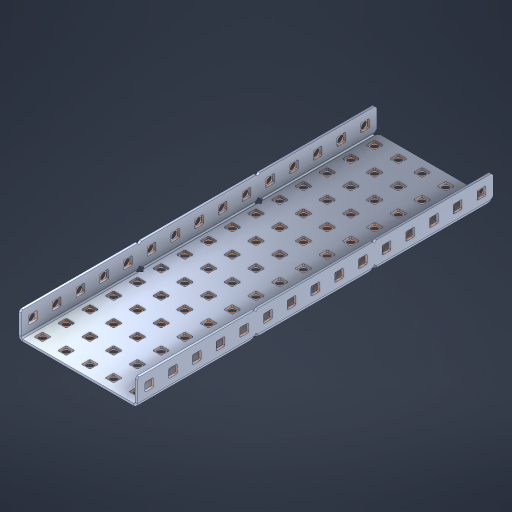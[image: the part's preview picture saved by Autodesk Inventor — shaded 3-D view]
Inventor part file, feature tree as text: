
AUTODESK INVENTOR PART (.ipt)
format: ipt  version: 2023 (Build 270158000, 158)  size: 1,352,192 bytes
history: native  units: in
note: dims shown in document units (in); Inventor stores cm internally (conversion verified against a paired STEP export)
features: other x110, extrude x104, sheet_metal_op x10, sketch x8, mirror x1, pattern_linear x1, chamfer x1
ambient origin geometry x8: Origin, YZ Plane, XZ Plane, XY Plane, X Axis, Y Axis, Z Axis, Center Point
bodies: Solid1 (feature_tree), Body (feature_tree)
feature tree (235):
  other  "Flange Pattern Plane"
  sheet_metal_op  "Flange Pattern"
  sheet_metal_op  "Body Pattern"
  other  "Arc Length"
  mirror  "Notch Mirror"
  pattern_linear  "Notch Pattern"  Spacing1=0.1875in  [1 undecoded]
  chamfer  "End Chamfer"
  extrude  "Half Cut"  Depth=0.0469in
  sketch  "Sketch1"  dims[d0=2.5in]
  other  "Plate1"
  sketch  "Sketch2"  dims[d1=7.5in]
  other  "Plate2"
  sheet_metal_op  "Bend1"
  sheet_metal_op  "Corner1"
  sketch  "Sketch3"  dims[d2=0.0469in]
  other  "Flange Pattern Sketch"
  sketch  "Sketch7"  dims[d3=0.0469in]
  other  "Srf1"
  other  "Srf2"
  sketch  "Sketch8"  dims[d4=0.0234in]
  sketch  "Sketch9"  dims[d5=0.0938in]
  other  "Srf91"
  sheet_metal_op  "Body Pattern Sketch"
  other  "Srf92"
  sketch  "Sketch13"  dims[d6=0.0469in]
  sketch  "Sketch14"  dims[d7=0.5in d8=90.0deg d9=0.0312in d10=0.1875in d11=0.0469in d12=0.0469in d16=0.182in d17=0.02in d18=0.0469in d19=0.0in d20=0.25in d21=0.25in d46=0.172in d47=1.0in d48=0.0in d49=0.182in d50=0.02in d51=0.25in d52=0.25in d53=0.0469in d54=0.0in d55=0.172in d56=1.0in d57=0.0in d60=5.9055in d62=0.5in d63=1.9685in d65=0.5in d85=0.1227in d86=0.1659in d88=0.04in d89=0.0469in d90=0.0in d91=0.04in d92=0.0491in d95=2.5in d96=0.04in d97=0.25in d98=45.0deg d101=0.0in d102=2.497in d131=2.5in d132=5.9055in d134=0.5in d139=0.5in]
  other  "Srf856"
  other  "Srf1310"
  other  "Srf1311"
  other  "Srf1312"
  other  "Srf1376"
  other  "Srf1377"
  other  "Srf1728"
  other  "Srf1755"
  other  "Srf1878"
  other  "Srf1879"
  other  "Srf1880"
  other  "Srf1881"
  other  "Srf1882"
  other  "Srf1883"
  other  "Srf1884"
  other  "Srf1885"
  other  "Srf1886"
  other  "Srf1887"
  other  "Srf1888"
  other  "Srf1889"
  other  "Srf1890"
  other  "Srf1891"
  other  "Srf1892"
  other  "Srf1893"
  other  "Srf1894"
  other  "Srf1895"
  other  "Srf1896"
  other  "Srf1897"
  other  "Srf1898"
  other  "Srf1899"
  other  "Srf1900"
  other  "Srf1901"
  other  "Srf1942"
  other  "Srf1943"
  other  "Srf1944"
  other  "Srf1945"
  other  "Srf1946"
  other  "Srf1947"
  other  "Srf1948"
  other  "Srf1949"
  other  "Srf1950"
  other  "Srf1951"
  other  "Srf1952"
  other  "Srf1953"
  other  "Srf1954"
  other  "Srf1955"
  other  "Srf1956"
  other  "Srf1957"
  other  "Srf1958"
  other  "Srf1959"
  other  "Srf1960"
  other  "Srf1961"
  other  "Srf1962"
  other  "Srf1963"
  other  "Srf1964"
  other  "Srf1965"
  other  "Srf1966"
  other  "Srf1967"
  other  "Srf1968"
  other  "Srf1969"
  other  "Srf1970"
  other  "Srf2146"
  other  "Srf2147"
  other  "Srf2148"
  other  "Srf2149"
  other  "Srf2150"
  other  "Srf2151"
  other  "Srf2152"
  other  "Srf2153"
  other  "Srf2154"
  other  "Srf2155"
  other  "Srf2156"
  other  "Srf2157"
  other  "Srf2158"
  other  "Srf2159"
  other  "Srf2160"
  other  "Srf2161"
  other  "Srf2162"
  other  "Srf2163"
  other  "Srf2164"
  other  "Srf2165"
  other  "Srf2166"
  other  "Srf2167"
  other  "Srf2168"
  other  "Srf2169"
  other  "Srf2170"
  other  "Srf2171"
  other  "Srf2172"
  other  "Srf2173"
  other  "Srf2174"
  other  "Srf2175"
  other  "Srf2176"
  other  "Srf2177"
  other  "Srf2178"
  other  "Srf2179"
  other  "Srf2180"
  other  "Srf2181"
  other  "Srf2182"
  other  "Srf2183"
  other  "Srf2184"
  other  "Srf2185"
  sheet_metal_op  "Flange Stamp"
  sheet_metal_op  "Flange Circle"
  sheet_metal_op  "Body Stamp"
  sheet_metal_op  "Body Circle"
  sheet_metal_op  "Notch"
  extrude  "ExtrusionSrf2"  Depth=0.0469in
  extrude  "ExtrusionSrf92"  Depth=2.5in
  extrude  "ExtrusionSrf856"  Depth=0.02in
  extrude  "ExtrusionSrf1310"  Depth=0.0469in
  extrude  "ExtrusionSrf1311"  TaperAngle=0.0deg  [1 undecoded]
  extrude  "ExtrusionSrf1312"  Depth=0.25in
  extrude  "ExtrusionSrf1376"  Depth=0.25in
  extrude  "ExtrusionSrf1377"  Depth=2.5in
  extrude  "ExtrusionSrf1728"  Depth=2.5in TaperAngle=0.0deg
  extrude  "ExtrusionSrf1755"  Depth=2.5in
  extrude  "ExtrusionSrf1878"  Depth=0.02in
  extrude  "ExtrusionSrf1879"  Depth=0.25in
  extrude  "ExtrusionSrf1880"  Depth=0.25in
  extrude  "ExtrusionSrf1881"  Depth=0.0469in
  extrude  "ExtrusionSrf1882"  TaperAngle=0.0deg  [1 undecoded]
  extrude  "ExtrusionSrf1883"  Depth=2.5in
  extrude  "ExtrusionSrf1884"  Depth=2.5in TaperAngle=0.0deg
  extrude  "ExtrusionSrf1885"  Depth=2.5in
  extrude  "ExtrusionSrf1886"  Depth=2.5in
  extrude  "ExtrusionSrf1887"  Depth=2.5in
  extrude  "ExtrusionSrf1888"  Depth=2.5in
  extrude  "ExtrusionSrf1889"  Depth=2.5in
  extrude  "ExtrusionSrf1890"  Depth=0.0469in
  extrude  "ExtrusionSrf1891"  TaperAngle=0.0deg  [1 undecoded]
  extrude  "ExtrusionSrf1892"  Depth=2.5in
  extrude  "ExtrusionSrf1893"  Depth=2.5in
  extrude  "ExtrusionSrf1894"  Depth=2.5in
  extrude  "ExtrusionSrf1895"  Depth=0.25in TaperAngle=45.0deg
  extrude  "ExtrusionSrf1896"  TaperAngle=0.0deg  [1 undecoded]
  extrude  "ExtrusionSrf1897"  Depth=2.5in
  extrude  "ExtrusionSrf1898"  Depth=2.5in
  extrude  "ExtrusionSrf1899"  Depth=2.5in
  extrude  "ExtrusionSrf1900"  Depth=2.5in
  extrude  "ExtrusionSrf1901"  Depth=2.5in
  extrude  "ExtrusionSrf1942"  [1 undecoded]
  extrude  "ExtrusionSrf1943"  [1 undecoded]
  extrude  "ExtrusionSrf1944"  [1 undecoded]
  extrude  "ExtrusionSrf1945"  [1 undecoded]
  extrude  "ExtrusionSrf1946"  [1 undecoded]
  extrude  "ExtrusionSrf1947"  [1 undecoded]
  extrude  "ExtrusionSrf1948"  [1 undecoded]
  extrude  "ExtrusionSrf1949"  [1 undecoded]
  extrude  "ExtrusionSrf1950"  [1 undecoded]
  extrude  "ExtrusionSrf1951"  [1 undecoded]
  extrude  "ExtrusionSrf1952"  [1 undecoded]
  extrude  "ExtrusionSrf1953"  [1 undecoded]
  extrude  "ExtrusionSrf1954"  [1 undecoded]
  extrude  "ExtrusionSrf1955"  [1 undecoded]
  extrude  "ExtrusionSrf1956"  [1 undecoded]
  extrude  "ExtrusionSrf1957"  [1 undecoded]
  extrude  "ExtrusionSrf1958"  [1 undecoded]
  extrude  "ExtrusionSrf1959"  [1 undecoded]
  extrude  "ExtrusionSrf1960"  [1 undecoded]
  extrude  "ExtrusionSrf1961"  [1 undecoded]
  extrude  "ExtrusionSrf1962"  [1 undecoded]
  extrude  "ExtrusionSrf1963"  [1 undecoded]
  extrude  "ExtrusionSrf1964"  [1 undecoded]
  extrude  "ExtrusionSrf1965"  [1 undecoded]
  extrude  "ExtrusionSrf1966"  [1 undecoded]
  extrude  "ExtrusionSrf1967"  [1 undecoded]
  extrude  "ExtrusionSrf1968"  [1 undecoded]
  extrude  "ExtrusionSrf1969"  [1 undecoded]
  extrude  "ExtrusionSrf1970"  [1 undecoded]
  extrude  "ExtrusionSrf2146"  [1 undecoded]
  extrude  "ExtrusionSrf2147"  [1 undecoded]
  extrude  "ExtrusionSrf2148"  [1 undecoded]
  extrude  "ExtrusionSrf2149"  [1 undecoded]
  extrude  "ExtrusionSrf2150"  [1 undecoded]
  extrude  "ExtrusionSrf2151"  [1 undecoded]
  extrude  "ExtrusionSrf2152"  [1 undecoded]
  extrude  "ExtrusionSrf2153"  [1 undecoded]
  extrude  "ExtrusionSrf2154"  [1 undecoded]
  extrude  "ExtrusionSrf2155"  [1 undecoded]
  extrude  "ExtrusionSrf2156"  [1 undecoded]
  extrude  "ExtrusionSrf2157"  [1 undecoded]
  extrude  "ExtrusionSrf2158"  [1 undecoded]
  extrude  "ExtrusionSrf2159"  [1 undecoded]
  extrude  "ExtrusionSrf2160"  [1 undecoded]
  extrude  "ExtrusionSrf2161"  [1 undecoded]
  extrude  "ExtrusionSrf2162"  [1 undecoded]
  extrude  "ExtrusionSrf2163"  [1 undecoded]
  extrude  "ExtrusionSrf2164"  [1 undecoded]
  extrude  "ExtrusionSrf2165"  [1 undecoded]
  extrude  "ExtrusionSrf2166"  [1 undecoded]
  extrude  "ExtrusionSrf2167"  [1 undecoded]
  extrude  "ExtrusionSrf2168"  [1 undecoded]
  extrude  "ExtrusionSrf2169"  [1 undecoded]
  extrude  "ExtrusionSrf2170"  [1 undecoded]
  extrude  "ExtrusionSrf2171"  [1 undecoded]
  extrude  "ExtrusionSrf2172"  [1 undecoded]
  extrude  "ExtrusionSrf2173"  [1 undecoded]
  extrude  "ExtrusionSrf2174"  [1 undecoded]
  extrude  "ExtrusionSrf2175"  [1 undecoded]
  extrude  "ExtrusionSrf2176"  [1 undecoded]
  extrude  "ExtrusionSrf2177"  [1 undecoded]
  extrude  "ExtrusionSrf2178"  [1 undecoded]
  extrude  "ExtrusionSrf2179"  [1 undecoded]
  extrude  "ExtrusionSrf2180"  [1 undecoded]
  extrude  "ExtrusionSrf2181"  [1 undecoded]
  extrude  "ExtrusionSrf2182"  [1 undecoded]
  extrude  "ExtrusionSrf2183"  [1 undecoded]
  extrude  "ExtrusionSrf2184"  [1 undecoded]
  extrude  "ExtrusionSrf2185"  [1 undecoded]
note: 74 required parameter values undecoded (feature->parameter linkage not recoverable at this tier; creation-order binding heuristic only, values carry confidence <= 0.55)
